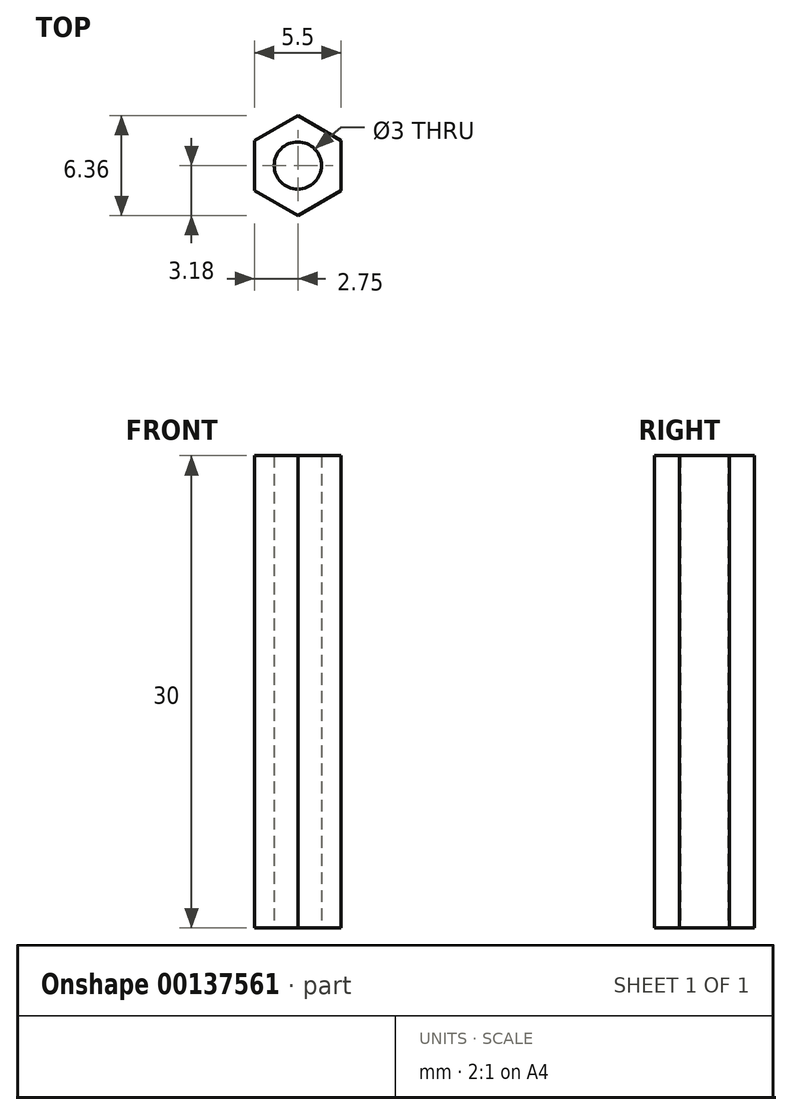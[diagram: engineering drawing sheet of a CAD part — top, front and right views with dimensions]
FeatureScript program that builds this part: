
annotation { "Feature Type Name" : "Feature", "Feature Type Description" : "" }
export const myFeature = defineFeature(function(context is Context, id is Id, definition is map)
    precondition{}
    {
        {
            var Q0;
            Q0=qCreatedBy(makeId("Top.planeOp"),FACE);
            var sketch = newSketch(context, id + "F0", { "sketchPlane" : qUnion([Q0])});
            skCircle(sketch, "E0.cCircle", {"center": v(0, 0) * mm, "radius": 2.75 * mm, "construction": true});
            skLineSegment(sketch, "E0.0", {"start": v(2.75, 1.59) * mm, "end": v(2.75, -1.59) * mm});
            skLineSegment(sketch, "E0.1", {"start": v(2.75, -1.59) * mm, "end": v(0, -3.18) * mm});
            skLineSegment(sketch, "E0.2", {"start": v(0, -3.18) * mm, "end": v(-2.75, -1.59) * mm});
            skLineSegment(sketch, "E0.3", {"start": v(-2.75, -1.59) * mm, "end": v(-2.75, 1.59) * mm});
            skLineSegment(sketch, "E0.4", {"start": v(-2.75, 1.59) * mm, "end": v(0, 3.18) * mm});
            skLineSegment(sketch, "E0.5", {"start": v(0, 3.18) * mm, "end": v(2.75, 1.59) * mm});
            skPoint(sketch, "E0.0.midPoint", {"position": v(2.75, 0) * mm});
            skCircle(sketch, "E1", {"center": v(0, 0) * mm, "radius": 1.5 * mm});
            skSolve(sketch);
        }
        {
            var Q0;
            Q0 = qSketchRegion(id + "F0", true);
            extrude(context, id + "F1", {"entities" : qUnion([Q0]), "depth" : 30 * mm});
        }
    });
